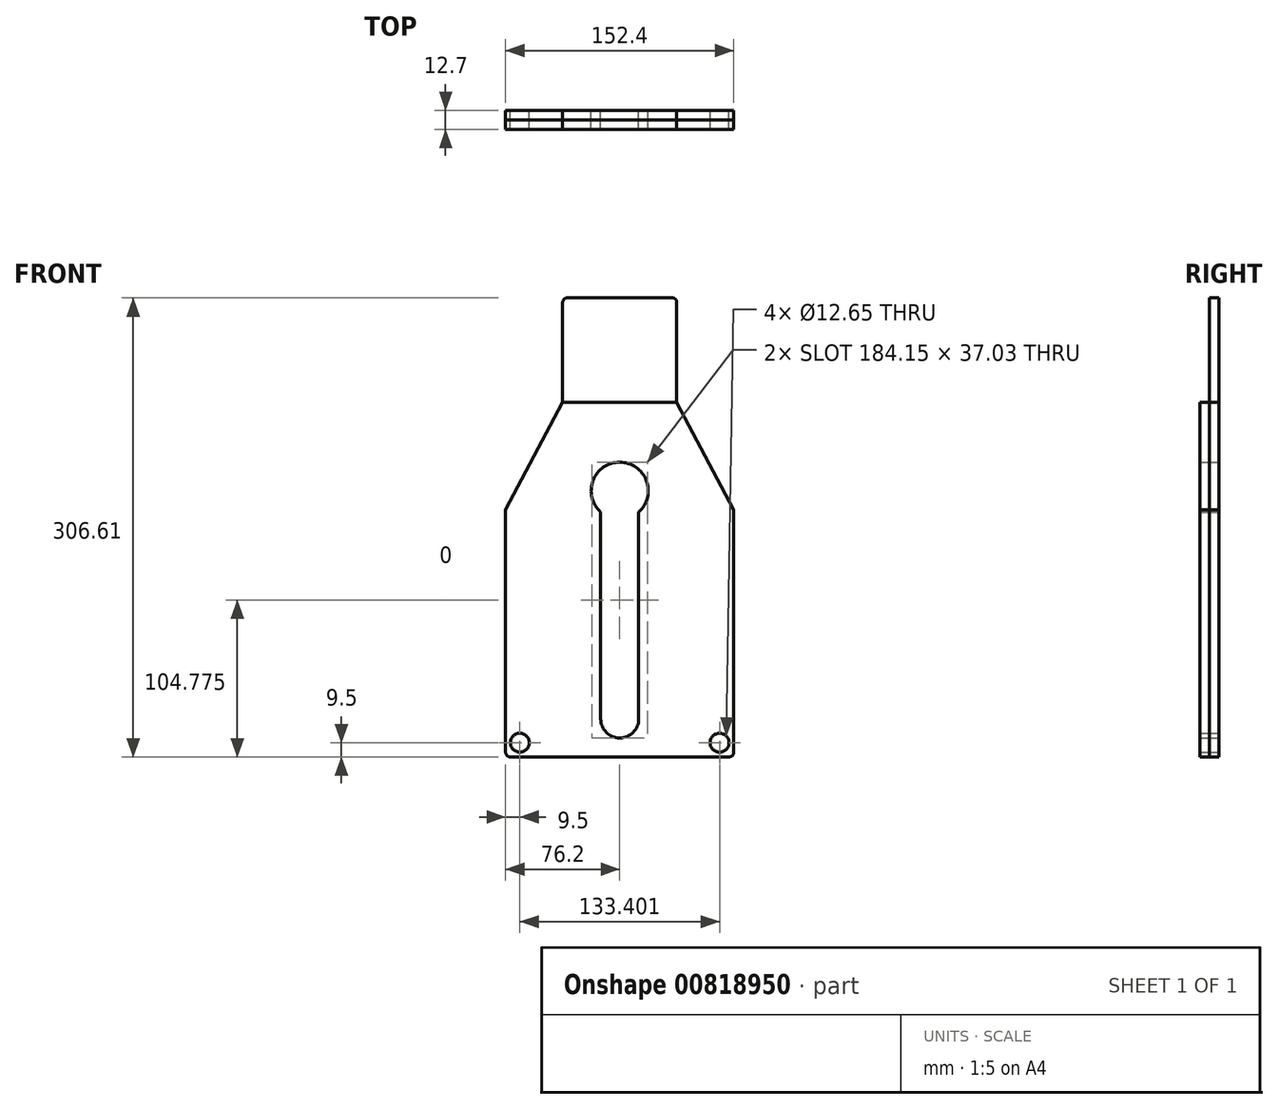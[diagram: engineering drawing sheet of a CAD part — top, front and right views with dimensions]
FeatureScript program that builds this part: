
annotation { "Feature Type Name" : "Feature", "Feature Type Description" : "" }
export const myFeature = defineFeature(function(context is Context, id is Id, definition is map)
    precondition{}
    {
        {
            var Q0;
            Q0=qCreatedBy(makeId("Front.planeOp"),FACE);
            var sketch = newSketch(context, id + "F0", { "sketchPlane" : qUnion([Q0])});
            skLineSegment(sketch, "E0", {"start": v(3.17, 0) * mm, "end": v(149.23, 0) * mm});
            skLineSegment(sketch, "E1", {"start": v(152.4, 3.18) * mm, "end": v(152.4, 165.1) * mm});
            skLineSegment(sketch, "E2", {"start": v(152.4, 165.1) * mm, "end": v(114.3, 236.76) * mm});
            skLineSegment(sketch, "E3", {"start": v(114.3, 236.76) * mm, "end": v(114.3, 303.68) * mm});
            skLineSegment(sketch, "E4", {"start": v(111.38, 306.6) * mm, "end": v(41.27, 306.6) * mm});
            skLineSegment(sketch, "E5", {"start": v(38.1, 303.43) * mm, "end": v(38.1, 236.76) * mm});
            skLineSegment(sketch, "E6", {"start": v(38.1, 236.76) * mm, "end": v(0, 165.1) * mm});
            skLineSegment(sketch, "E7", {"start": v(0, 165.1) * mm, "end": v(0, 3.17) * mm});
            skLineSegment(sketch, "E8", {"start": v(76.2, 306.6) * mm, "end": v(76.2, 0) * mm, "construction": true});
            skArc(sketch, "E9", {"start": v(88.9, 163.6) * mm, "mid": v(76.2, 196.85) * mm, "end": v(63.5, 163.6) * mm});
            skArc(sketch, "E10", {"start": v(63.5, 25.4) * mm, "mid": v(76.2, 12.7) * mm, "end": v(88.9, 25.4) * mm});
            skLineSegment(sketch, "E11", {"start": v(63.5, 25.4) * mm, "end": v(63.5, 163.6) * mm});
            skLineSegment(sketch, "E12", {"start": v(88.9, 25.4) * mm, "end": v(88.9, 163.6) * mm});
            skPoint(sketch, "E13.visualSharp", {"position": v(152.4, 0) * mm});
            skArc(sketch, "E13.filletArc", {"start": v(149.23, 0) * mm, "mid": v(151.47, 0.93) * mm, "end": v(152.4, 3.18) * mm});
            skPoint(sketch, "E14.visualSharp", {"position": v(0, 0) * mm});
            skArc(sketch, "E14.filletArc", {"start": v(0, 3.17) * mm, "mid": v(0.93, 0.93) * mm, "end": v(3.17, 0) * mm});
            skPoint(sketch, "E15.visualSharp", {"position": v(114.3, 306.6) * mm});
            skArc(sketch, "E15.filletArc", {"start": v(114.3, 303.68) * mm, "mid": v(113.44, 305.75) * mm, "end": v(111.38, 306.6) * mm});
            skPoint(sketch, "E16.visualSharp", {"position": v(38.1, 306.6) * mm});
            skArc(sketch, "E16.filletArc", {"start": v(41.27, 306.6) * mm, "mid": v(39.03, 305.68) * mm, "end": v(38.1, 303.43) * mm});
            skCircle(sketch, "E17", {"center": v(142.9, 9.5) * mm, "radius": 6.32 * mm});
            skCircle(sketch, "E18.MirrorC", {"center": v(9.5, 9.5) * mm, "radius": 6.32 * mm});
            skSolve(sketch);
        }
        {
            var Q0;
            Q0 = qSketchRegion(id + "F0", true);
            extrude(context, id + "F1", {"entities" : qUnion([Q0]), "depth" : 6.35 * mm, "offsetDistance" : 25.4 * mm});
        }
        {
            var Q0;
            Q0=makeQuery(id+"F1.opExtrude","CAP_FACE",FACE,{"disambiguationData":[OSD([sQuery(id+"F0.wireOp",EDGE,"E0"),sQuery(id+"F0.wireOp",EDGE,"E1"),sQuery(id+"F0.wireOp",EDGE,"E2"),sQuery(id+"F0.wireOp",EDGE,"E3"),sQuery(id+"F0.wireOp",EDGE,"E4"),sQuery(id+"F0.wireOp",EDGE,"E5"),sQuery(id+"F0.wireOp",EDGE,"E6"),sQuery(id+"F0.wireOp",EDGE,"E7"),sQuery(id+"F0.wireOp",EDGE,"E9"),sQuery(id+"F0.wireOp",EDGE,"E10"),sQuery(id+"F0.wireOp",EDGE,"E11"),sQuery(id+"F0.wireOp",EDGE,"E12"),sQuery(id+"F0.wireOp",EDGE,"E13.filletArc"),sQuery(id+"F0.wireOp",EDGE,"E14.filletArc"),sQuery(id+"F0.wireOp",EDGE,"E15.filletArc"),sQuery(id+"F0.wireOp",EDGE,"E16.filletArc"),sQuery(id+"F0.wireOp",EDGE,"E17"),sQuery(id+"F0.wireOp",EDGE,"E18.MirrorC")])],"isStart":false});
            var sketch = newSketch(context, id + "F2", { "sketchPlane" : qUnion([Q0])});
            skLineSegment(sketch, "E19.bottom", {"start": v(152.4, 0) * mm, "end": v(0, 0) * mm});
            skLineSegment(sketch, "E19.top", {"start": v(152.4, 236.76) * mm, "end": v(0, 236.76) * mm});
            skLineSegment(sketch, "E19.left", {"start": v(152.4, 0) * mm, "end": v(152.4, 236.76) * mm});
            skLineSegment(sketch, "E19.right", {"start": v(0, 0) * mm, "end": v(0, 236.76) * mm});
            skSolve(sketch);
        }
        {
            var Q0;
            {var subQ1=makeQuery(id+"F1.opExtrude","CAP_EDGE",EDGE,{"disambiguationData":[OSD([sQuery(id+"F0.wireOp",EDGE,"E2")])],"isStart":false});Q0=makeQuery(id+"F2.imprint","IMPRINT",FACE,{"disambiguationData":[TD([[makeQuery(id+"F2.imprint","IMPRINT",EDGE,{"derivedFrom":subQ1}),1.0]])]});}
            extrude(context, id + "F3", {"entities" : qUnion([Q0]), "depth" : 6.35 * mm, "offsetDistance" : 25.4 * mm});
        }
    });
